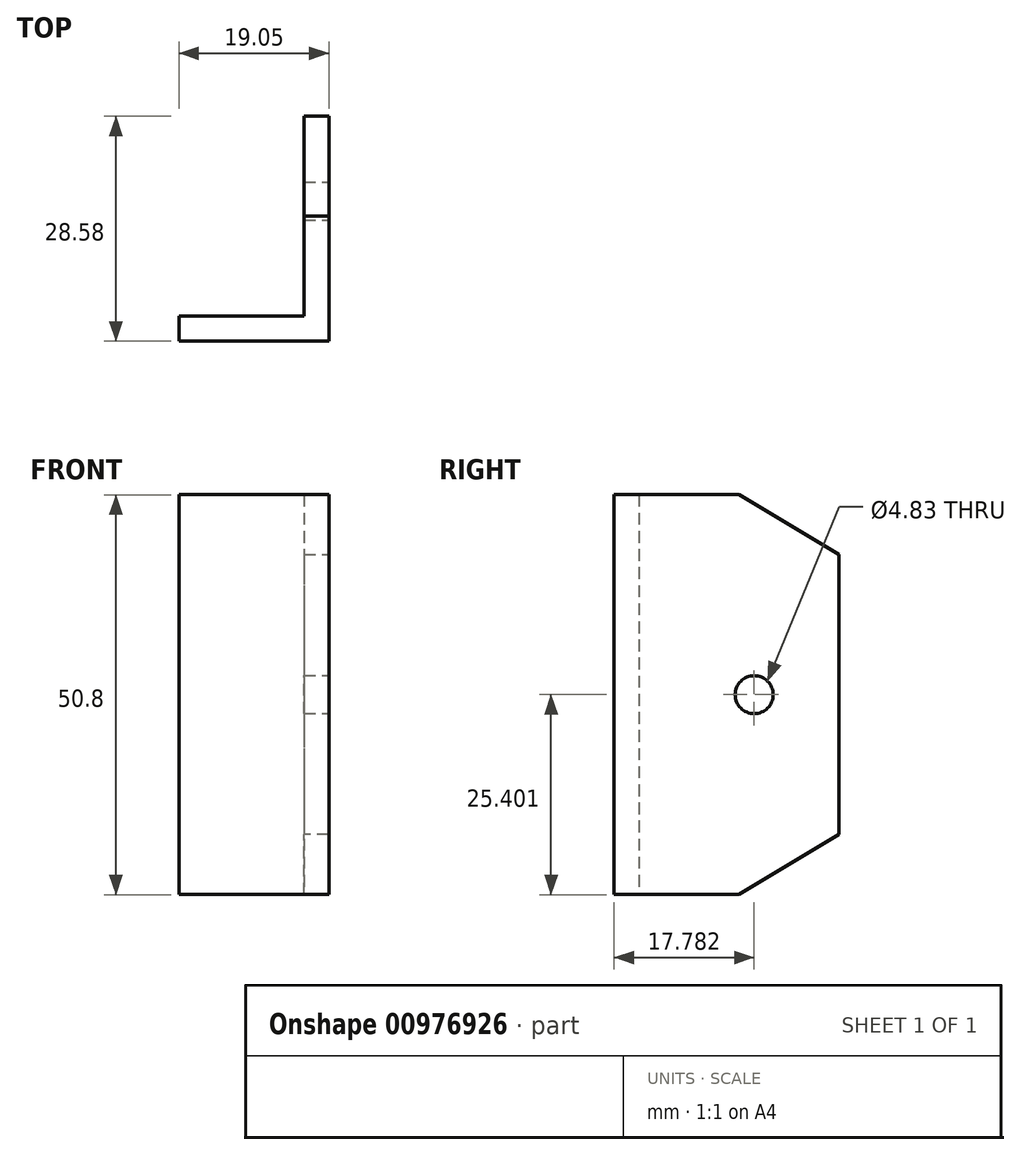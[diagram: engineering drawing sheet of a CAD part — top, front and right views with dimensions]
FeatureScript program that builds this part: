
annotation { "Feature Type Name" : "Feature", "Feature Type Description" : "" }
export const myFeature = defineFeature(function(context is Context, id is Id, definition is map)
    precondition{}
    {
        {
            var Q0;
            Q0=qCreatedBy(makeId("Front.planeOp"),FACE);
            var sketch = newSketch(context, id + "F0", { "sketchPlane" : qUnion([Q0])});
            skLineSegment(sketch, "E0.bottom", {"start": v(-8.02, 20.58) * mm, "end": v(11.03, 20.58) * mm});
            skLineSegment(sketch, "E0.top", {"start": v(-8.02, -30.22) * mm, "end": v(11.03, -30.22) * mm});
            skLineSegment(sketch, "E0.left", {"start": v(-8.02, 20.58) * mm, "end": v(-8.02, -30.22) * mm});
            skLineSegment(sketch, "E0.right", {"start": v(11.03, 20.58) * mm, "end": v(11.03, -30.22) * mm});
            skSolve(sketch);
        }
        {
            var Q0;
            Q0 = qSketchRegion(id + "F0", true);
            extrude(context, id + "F1", {"entities" : qUnion([Q0]), "endBound" : BoundingType.SYMMETRIC, "depth" : 28.57 * mm, "offsetDistance" : 25.4 * mm});
        }
        {
            var Q0;
            Q0=makeQuery(id+"F1.opExtrude","SWEPT_FACE",FACE,{"disambiguationData":[OSD([sQuery(id+"F0.wireOp",EDGE,"E0.left")])]});
            var Q1;
            Q1=makeQuery(id+"F1.opExtrude","SWEPT_FACE",FACE,{"disambiguationData":[OSD([sQuery(id+"F0.wireOp",EDGE,"E0.top")])]});
            var Q2;
            Q2=makeQuery(id+"F1.opExtrude","CAP_FACE",FACE,{"disambiguationData":[OSD([sQuery(id+"F0.wireOp",EDGE,"E0.bottom"),sQuery(id+"F0.wireOp",EDGE,"E0.top"),sQuery(id+"F0.wireOp",EDGE,"E0.left"),sQuery(id+"F0.wireOp",EDGE,"E0.right")])],"isStart":true});
            var Q3;
            Q3=makeQuery(id+"F1.opExtrude","SWEPT_FACE",FACE,{"disambiguationData":[OSD([sQuery(id+"F0.wireOp",EDGE,"E0.bottom")])]});
            shell(context, id + "F2", {"entities" : qUnion([Q0, Q1, Q2, Q3]), "thickness" : 3.17 * mm});
        }
        {
            var Q0;
            Q0=makeQuery(id+"F1.opExtrude","SWEPT_FACE",FACE,{"disambiguationData":[OSD([sQuery(id+"F0.wireOp",EDGE,"E0.right")])]});
            var sketch = newSketch(context, id + "F3", { "sketchPlane" : qUnion([Q0])});
            skPoint(sketch, "E1", {"position": v(3.5, -4.82) * mm});
            skSolve(sketch);
        }
        {
            var Q0;
            Q0=sQuery(id+"F3.wireOp",VERTEX,"E1");
            var Q1;
            Q1=makeQuery(id+"F1.opExtrude","SWEPT_BODY",BODY,{"disambiguationData":[OSD([sQuery(id+"F0.wireOp",EDGE,"E0.bottom"),sQuery(id+"F0.wireOp",EDGE,"E0.top"),sQuery(id+"F0.wireOp",EDGE,"E0.left"),sQuery(id+"F0.wireOp",EDGE,"E0.right")])]});
            hole(context, id + "F4", {"style" : HoleStyle.SIMPLE, "endStyle" : HoleEndStyle.THROUGH, "holeDiameter" : 4.83 * mm, "majorDiameter" : 6.35 * mm, "isTappedThrough" : true, "tappedDepth" : 12.7 * mm, "tapClearance" : 3, "locations" : qUnion([Q0]), "scope" : qUnion([Q1])});
        }
        {
            var Q0;
            Q0=makeQuery(id+"F1.opExtrude","CAP_EDGE",EDGE,{"disambiguationData":[OSD([sQuery(id+"F0.wireOp",EDGE,"E0.top")])],"isStart":true});
            var Q1;
            Q1=makeQuery(id+"F1.opExtrude","CAP_EDGE",EDGE,{"disambiguationData":[OSD([sQuery(id+"F0.wireOp",EDGE,"E0.bottom")])],"isStart":true});
            chamfer(context, id + "F5", {"entities" : qUnion([Q0, Q1]), "chamferType" : ChamferType.TWO_OFFSETS, "width1" : 12.7 * mm, "oppositeDirection" : false, "width2" : 7.62 * mm, "tangentPropagation" : true});
        }
    });
